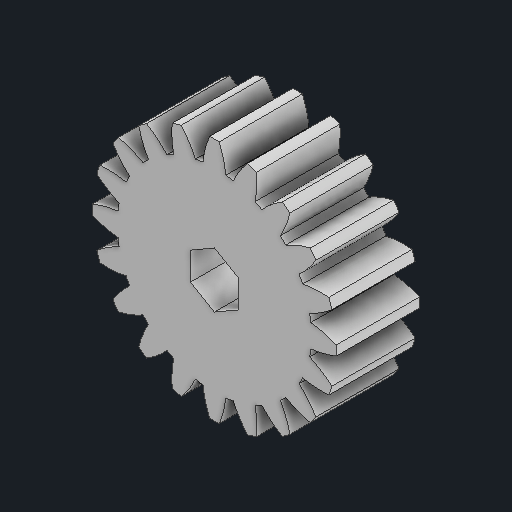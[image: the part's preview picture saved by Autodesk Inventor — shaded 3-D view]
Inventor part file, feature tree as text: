
AUTODESK INVENTOR PART (.ipt)
format: ipt  version: 2024 (Build 280153000, 153)  size: 230,400 bytes
history: native  units: mm
features: other x4, extrude x1, sketch x1
ambient origin geometry x8: Origin, YZ Plane, XZ Plane, XY Plane, X Axis, Y Axis, Z Axis, Center Point
bodies: Body1 (feature_tree)
feature tree (6):
  other  "{BB8FE430-83BF-418D-8DF9-9B323D3DB9B9}"
  other  "솔리드1"
  extrude  "돌출1"  Depth=44.0mm
  other  "스퍼 기어 톱니1"
  sketch  "스케치1"
  other  "스퍼 기어1"
